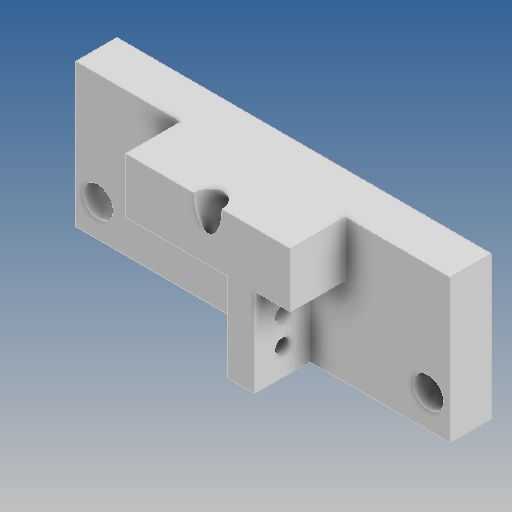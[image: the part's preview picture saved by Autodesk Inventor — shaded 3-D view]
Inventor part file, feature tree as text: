
AUTODESK INVENTOR PART (.ipt)
format: ipt  version: 2020 (Build 240168000, 168)  size: 169,472 bytes
history: native  units: mm
features: sketch x7, extrude x5, reference x3, hole x2, other x2, plane x1, projected_geometry x1
ambient origin geometry x8: Origin, YZ Plane, XZ Plane, XY Plane, X Axis, Y Axis, Z Axis, Center Point
bodies: Solid1 (feature_tree)
feature tree (21):
  extrude  "Extrusion1"  Depth=52.0mm
  hole  "Hole3"  [1 undecoded]
  extrude  "Extrusion6"  TaperAngle=30.0deg  [1 undecoded]
  plane  "Work Plane1"
  extrude  "Extrusion7"  Depth=10.0mm
  extrude  "Extrusion8"  Depth=20.0mm
  extrude  "Extrusion9"  Depth=10.0mm
  hole  "Hole4"  [1 undecoded]
  sketch  "Sketch1"  dims[d0=136.0mm d1=52.0mm]
  sketch  "Sketch9"  dims[d2=15.0mm d3=0.0mm]
  reference  "Reference12"
  reference  "Reference13"
  reference  "Reference14"
  sketch  "Sketch10"  dims[d40=11.0mm d41=6.0mm d42=4.0mm d43=2.0mm d44=90.0deg d45=8.0mm d46=20.594885mm d47=60.0mm]
  sketch  "Sketch11"  dims[d48=20.0mm d49=0.0mm d51=30.0deg]
  sketch  "Sketch12"  dims[d52=10.0mm d53=10.0mm]
  projected_geometry  "Projected Loop1"
  sketch  "Sketch13"  dims[d54=33.0mm d55=0.0mm d56=20.0mm]
  sketch  "Sketch14"  dims[d57=33.0mm d58=0.0mm d59=10.0mm d62=2.0mm d63=33.0mm d64=0.0mm d65=10.0mm d66=10.0mm d67=5.0mm d68=6.0mm d69=4.0mm d70=2.0mm d71=90.0deg d72=8.0mm d73=20.594885mm d60=0.872665mm]
  other  "30-00 Injectomat suplimentar.iam"
  other  "I.A.B 2.1 Aracet_Subansamble_Shrinkwrap_2:1"
note: 3 required parameter values undecoded (feature->parameter linkage not recoverable at this tier; creation-order binding heuristic only, values carry confidence <= 0.55)
